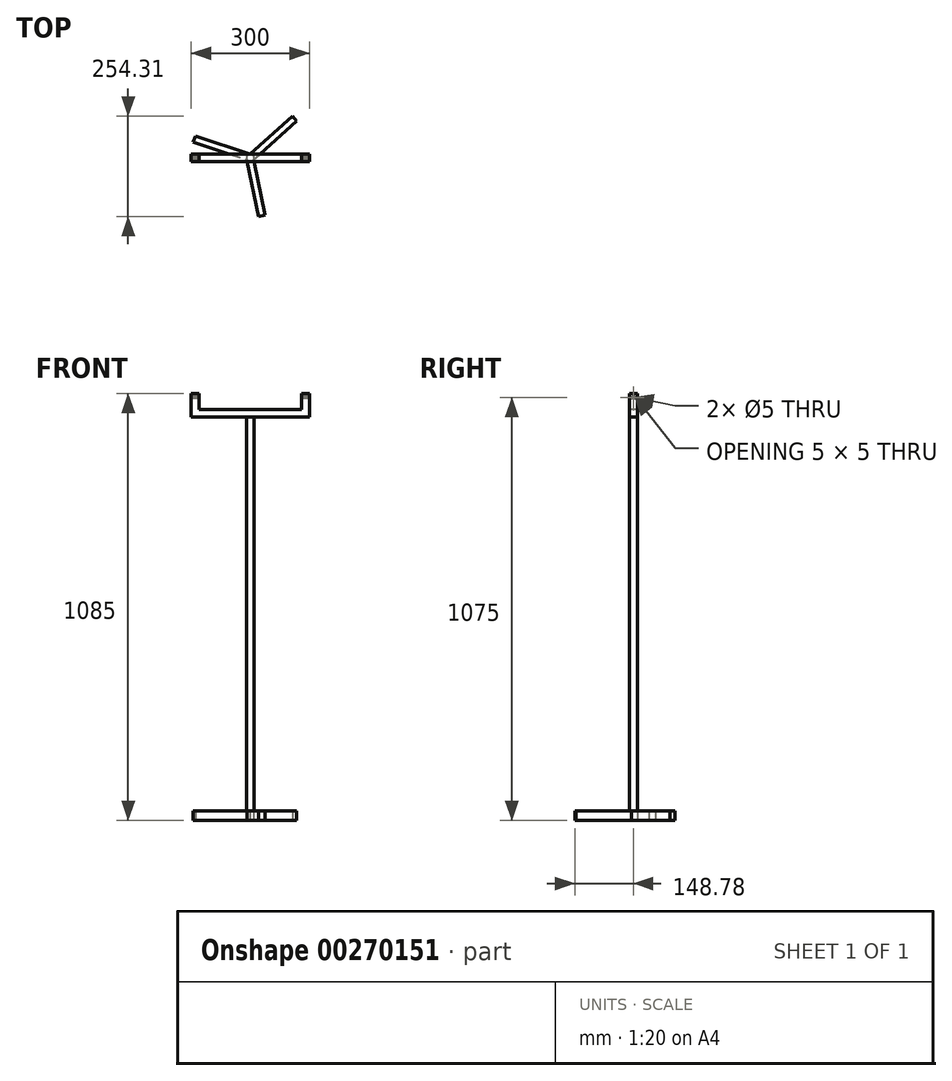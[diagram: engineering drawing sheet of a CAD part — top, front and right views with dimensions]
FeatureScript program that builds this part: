
annotation { "Feature Type Name" : "Feature", "Feature Type Description" : "" }
export const myFeature = defineFeature(function(context is Context, id is Id, definition is map)
    precondition{}
    {
        {
            var Q0;
            Q0=qCreatedBy(makeId("Top.planeOp"),FACE);
            var sketch = newSketch(context, id + "F0", { "sketchPlane" : qUnion([Q0])});
            skArc(sketch, "E0", {"start": v(8.66, -5) * mm, "mid": v(8.68, -4.97) * mm, "end": v(8.7, -4.94) * mm});
            skLineSegment(sketch, "E1", {"start": v(0, 10) * mm, "end": v(-139.5, 55.93) * mm});
            skLineSegment(sketch, "E2", {"start": v(-139.5, 55.93) * mm, "end": v(-144.82, 39.79) * mm});
            skLineSegment(sketch, "E3", {"start": v(-144.82, 39.79) * mm, "end": v(-8.63, -5.06) * mm});
            skLineSegment(sketch, "E4.1.0", {"start": v(21.31, -148.78) * mm, "end": v(37.95, -145.31) * mm});
            skLineSegment(sketch, "E4.1.1", {"start": v(-8.66, -5) * mm, "end": v(21.31, -148.78) * mm});
            skLineSegment(sketch, "E4.1.2", {"start": v(37.95, -145.31) * mm, "end": v(8.7, -4.94) * mm});
            skLineSegment(sketch, "E4.2.0", {"start": v(118.2, 92.85) * mm, "end": v(106.87, 105.53) * mm});
            skLineSegment(sketch, "E4.2.1", {"start": v(8.66, -5) * mm, "end": v(118.2, 92.85) * mm});
            skLineSegment(sketch, "E4.2.2", {"start": v(106.87, 105.53) * mm, "end": v(-0.07, 10) * mm});
            skArc(sketch, "E5.trimOffspring", {"start": v(-8.66, -5) * mm, "mid": v(-8.64, -5.03) * mm, "end": v(-8.63, -5.06) * mm});
            skArc(sketch, "E6.trimOffspring", {"start": v(0, 10) * mm, "mid": v(-0.03, 10) * mm, "end": v(-0.07, 10) * mm});
            skSolve(sketch);
        }
        {
            var Q0;
            Q0 = qSketchRegion(id + "F0", true);
            extrude(context, id + "F1", {"entities" : qUnion([Q0]), "depth" : 25 * mm});
        }
        {
            var Q0;
            Q0=makeQuery(id+"F1.opExtrude","CAP_FACE",FACE,{"disambiguationData":[OSD([sQuery(id+"F0.wireOp",EDGE,"E0"),sQuery(id+"F0.wireOp",EDGE,"E1"),sQuery(id+"F0.wireOp",EDGE,"E2"),sQuery(id+"F0.wireOp",EDGE,"E3"),sQuery(id+"F0.wireOp",EDGE,"E4.1.0"),sQuery(id+"F0.wireOp",EDGE,"E4.1.1"),sQuery(id+"F0.wireOp",EDGE,"E4.1.2"),sQuery(id+"F0.wireOp",EDGE,"E4.2.0"),sQuery(id+"F0.wireOp",EDGE,"E4.2.1"),sQuery(id+"F0.wireOp",EDGE,"E4.2.2")])],"isStart":false});
            var sketch = newSketch(context, id + "F2", { "sketchPlane" : qUnion([Q0])});
            skCircle(sketch, "E7", {"center": v(0, 0) * mm, "radius": 10 * mm});
            skSolve(sketch);
        }
        {
            var Q0;
            Q0 = qSketchRegion(id + "F2", true);
            extrude(context, id + "F3", {"entities" : qUnion([Q0]), "depth" : 1000 * mm});
        }
        {
            var Q0;
            Q0=makeQuery(id+"F3.opExtrude","CAP_FACE",FACE,{"disambiguationData":[OSD([sQuery(id+"F2.wireOp",EDGE,"E7")])],"isStart":false});
            var sketch = newSketch(context, id + "F4", { "sketchPlane" : qUnion([Q0])});
            skLineSegment(sketch, "E8.bottom", {"start": v(150, -10) * mm, "end": v(-150, -10) * mm});
            skLineSegment(sketch, "E8.top", {"start": v(150, 10) * mm, "end": v(-150, 10) * mm});
            skLineSegment(sketch, "E8.left", {"start": v(150, -10) * mm, "end": v(150, 10) * mm});
            skLineSegment(sketch, "E8.right", {"start": v(-150, -10) * mm, "end": v(-150, 10) * mm});
            skPoint(sketch, "E8.middle", {"position": v(0, 0) * mm});
            skSolve(sketch);
        }
        {
            var Q0;
            Q0 = qSketchRegion(id + "F4", true);
            extrude(context, id + "F5", {"entities" : qUnion([Q0]), "operationType" : NewBodyOperationType.ADD, "depth" : 20 * mm});
        }
        {
            var Q0;
            Q0=makeQuery(id+"F5.opExtrude","CAP_FACE",FACE,{"disambiguationData":[OSD([sQuery(id+"F4.wireOp",EDGE,"E8.bottom"),sQuery(id+"F4.wireOp",EDGE,"E8.top"),sQuery(id+"F4.wireOp",EDGE,"E8.left"),sQuery(id+"F4.wireOp",EDGE,"E8.right")])],"isStart":false});
            var sketch = newSketch(context, id + "F6", { "sketchPlane" : qUnion([Q0])});
            skLineSegment(sketch, "E9.bottom", {"start": v(-150, 10) * mm, "end": v(-130, 10) * mm});
            skLineSegment(sketch, "E9.top", {"start": v(-150, -10) * mm, "end": v(-130, -10) * mm});
            skLineSegment(sketch, "E9.left", {"start": v(-150, 10) * mm, "end": v(-150, -10) * mm});
            skLineSegment(sketch, "E9.right", {"start": v(-130, 10) * mm, "end": v(-130, -10) * mm});
            skLineSegment(sketch, "E10.bottom", {"start": v(150, 10) * mm, "end": v(130, 10) * mm});
            skLineSegment(sketch, "E10.top", {"start": v(150, -10) * mm, "end": v(130, -10) * mm});
            skLineSegment(sketch, "E10.left", {"start": v(150, 10) * mm, "end": v(150, -10) * mm});
            skLineSegment(sketch, "E10.right", {"start": v(130, 10) * mm, "end": v(130, -10) * mm});
            skSolve(sketch);
        }
        {
            var Q0;
            Q0 = qSketchRegion(id + "F6", true);
            extrude(context, id + "F7", {"entities" : qUnion([Q0]), "operationType" : NewBodyOperationType.ADD, "depth" : 40 * mm});
        }
        {
            var Q0;
            Q0=makeQuery(id+"F7.boolean.opBoolean","MERGE",FACE,{"derivedFrom":[makeQuery(id+"F5.opExtrude","SWEPT_FACE",FACE,{"disambiguationData":[OSD([sQuery(id+"F4.wireOp",EDGE,"E8.right")])]}),makeQuery(id+"F7.opExtrude","SWEPT_FACE",FACE,{"disambiguationData":[OSD([sQuery(id+"F6.wireOp",EDGE,"E9.left")])]})]});
            var sketch = newSketch(context, id + "F8", { "sketchPlane" : qUnion([Q0])});
            skCircle(sketch, "E11", {"center": v(0, 1075) * mm, "radius": 2.5 * mm});
            skSolve(sketch);
        }
        {
            var Q0;
            Q0 = qSketchRegion(id + "F8", true);
            extrude(context, id + "F9", {"entities" : qUnion([Q0]), "operationType" : NewBodyOperationType.REMOVE, "oppositeDirection" : true, "depth" : 500 * mm});
        }
    });
